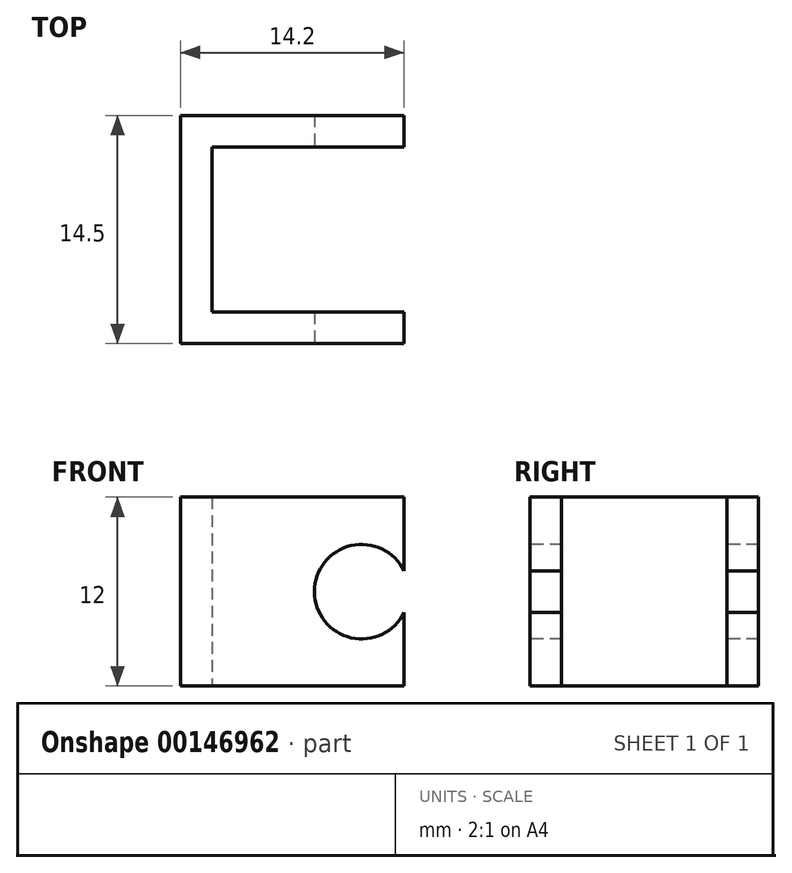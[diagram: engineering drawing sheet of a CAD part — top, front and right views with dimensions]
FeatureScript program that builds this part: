
annotation { "Feature Type Name" : "Feature", "Feature Type Description" : "" }
export const myFeature = defineFeature(function(context is Context, id is Id, definition is map)
    precondition{}
    {
        {
            var Q0;
            Q0=qCreatedBy(makeId("Top.planeOp"),FACE);
            var sketch = newSketch(context, id + "F0", { "sketchPlane" : qUnion([Q0])});
            skLineSegment(sketch, "E0", {"start": v(0, 0) * mm, "end": v(-12.2, 0) * mm});
            skLineSegment(sketch, "E1", {"start": v(-12.2, 0) * mm, "end": v(-12.2, 10.5) * mm});
            skLineSegment(sketch, "E2", {"start": v(-12.2, 10.5) * mm, "end": v(0, 10.5) * mm});
            skLineSegment(sketch, "E3", {"start": v(0, 10.5) * mm, "end": v(0, 12.5) * mm});
            skLineSegment(sketch, "E4", {"start": v(0, 12.5) * mm, "end": v(-14.2, 12.5) * mm});
            skLineSegment(sketch, "E5", {"start": v(-14.2, 12.5) * mm, "end": v(-14.2, -2) * mm});
            skLineSegment(sketch, "E6", {"start": v(-14.2, -2) * mm, "end": v(0, -2) * mm});
            skLineSegment(sketch, "E7", {"start": v(0, -2) * mm, "end": v(0, 0) * mm});
            skSolve(sketch);
        }
        {
            var Q0;
            Q0 = qSketchRegion(id + "F0", true);
            extrude(context, id + "F1", {"entities" : qUnion([Q0]), "depth" : 12 * mm});
        }
        {
            var Q0;
            Q0=makeQuery(id+"F1.opExtrude","SWEPT_FACE",FACE,{"disambiguationData":[OSD([sQuery(id+"F0.wireOp",EDGE,"E6")])]});
            var sketch = newSketch(context, id + "F2", { "sketchPlane" : qUnion([Q0])});
            skLineSegment(sketch, "E8", {"start": v(-14.2, 6) * mm, "end": v(-2.7, 6) * mm, "construction": true});
            skCircle(sketch, "E9", {"center": v(-2.7, 6) * mm, "radius": 3 * mm});
            skSolve(sketch);
        }
        {
            var Q0;
            Q0=makeQuery(id+"F2.imprint","IMPRINT",FACE,{"disambiguationData":[TD([[makeQuery(id+"F2.imprint","IMPRINT",EDGE,{"derivedFrom":sQuery(id+"F2.wireOp",EDGE,"E9")}),1.0]])]});
            extrude(context, id + "F3", {"entities" : qUnion([Q0]), "operationType" : NewBodyOperationType.REMOVE, "endBound" : BoundingType.SYMMETRIC, "oppositeDirection" : true, "depth" : 66 * mm});
        }
    });
